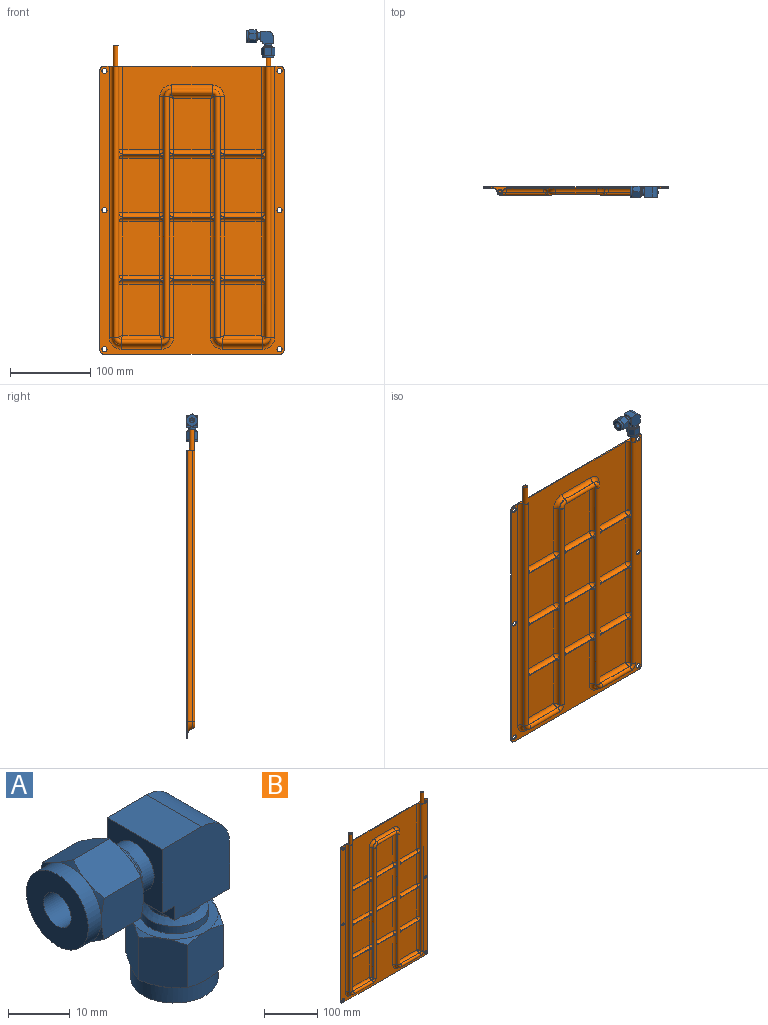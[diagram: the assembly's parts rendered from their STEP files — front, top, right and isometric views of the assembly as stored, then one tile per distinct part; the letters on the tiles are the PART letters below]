
ASSEMBLY  parts=2 mates=1
PART A: 64 faces, bbox 35.1x16.4x35.1 mm
  f0: cylinder r=3.17mm len=15.24mm, axis (1,0,0), area 304mm2, adj f1,f2
  f1: plane 6.35x6.35mm, normal (-1,0,0), area 13.4mm2, adj f0,f3
  f2: plane 14.22x14.22mm, normal (-1,0,0), area 127.2mm2, adj f0,f5
  f3: cylinder r=2.41mm len=11.68mm, axis (1,0,0), area 165.5mm2, adj f1,f4,f6
  f4: sphere r=2.41mm, area 18.3mm2, adj f3,f6
  f5: cylinder r=7.11mm len=14.22mm, axis (1,0,0), area 136.2mm2, adj f2,f7,f8,f9,f10,f11,f12
  f6: cylinder r=2.41mm len=11.68mm, axis (0,0,-1), area 165.5mm2, adj f3,f4,f13
  f7: cone r=7.66mm half-angle=60deg, axis (1,0,0), area 3.1mm2, adj f5,f14,f15
  f8: cone r=7.66mm half-angle=60deg, axis (1,0,0), area 3.1mm2, adj f5,f15,f16
  f9: cone r=7.66mm half-angle=60deg, axis (1,0,0), area 3.1mm2, adj f5,f16,f17
  f10: cone r=7.66mm half-angle=60deg, axis (1,0,0), area 3.1mm2, adj f5,f17,f18
  f11: cone r=7.66mm half-angle=60deg, axis (1,0,0), area 3.1mm2, adj f5,f18,f19
  f12: cone r=7.66mm half-angle=60deg, axis (1,0,0), area 3.1mm2, adj f5,f14,f19
  f13: plane 6.35x6.35mm, normal (0,0,-1), area 13.4mm2, adj f6,f20
  f14: plane 9.65x8.21mm, normal (0,1,0), area 75.7mm2, adj f7,f12,f15,f19,f21,f22
  f15: plane 9.65x7.11mm, normal (0,0.5,-0.87), area 75.7mm2, adj f7,f8,f14,f16,f22,f23
  f16: plane 9.65x7.11mm, normal (0,-0.5,-0.87), area 75.7mm2, adj f8,f9,f15,f17,f23,f24
  f17: plane 9.65x8.21mm, normal (0,-1,0), area 75.7mm2, adj f9,f10,f16,f18,f24,f25
  f18: plane 9.65x7.11mm, normal (0,-0.5,0.87), area 75.7mm2, adj f10,f11,f17,f19,f25,f26
  f19: plane 9.65x7.11mm, normal (0,0.5,0.87), area 75.7mm2, adj f11,f12,f14,f18,f21,f26
  f20: cylinder r=3.17mm len=15.24mm, axis (0,0,1), area 304mm2, adj f13,f27
  f21: cone r=7.66mm half-angle=60deg, axis (-1,0,0), area 3.1mm2, adj f14,f19,f28
  f22: cone r=7.66mm half-angle=60deg, axis (-1,0,0), area 3.1mm2, adj f14,f15,f28
  f23: cone r=7.66mm half-angle=60deg, axis (-1,0,0), area 3.1mm2, adj f15,f16,f28
  f24: cone r=7.66mm half-angle=60deg, axis (-1,0,0), area 3.1mm2, adj f16,f17,f28
  f25: cone r=7.66mm half-angle=60deg, axis (-1,0,0), area 3.1mm2, adj f17,f18,f28
  f26: cone r=7.66mm half-angle=60deg, axis (-1,0,0), area 3.1mm2, adj f18,f19,f28
  f27: plane 14.22x14.22mm, normal (0,0,-1), area 127.2mm2, adj f20,f29
  f28: plane 14.22x14.22mm, normal (1,0,0), area 61.9mm2, adj f21,f22,f23,f24,f25,f26,f30
  f29: cylinder r=7.11mm len=14.22mm, axis (0,0,1), area 136.2mm2, adj f27,f31,f32,f33,f34,f35,f36
  f30: cylinder r=5.56mm len=11.11mm, axis (1,0,0), area 51mm2, adj f28,f37
  f31: cone r=7.66mm half-angle=60deg, axis (0,0,1), area 3.1mm2, adj f29,f38,f39
  f32: cone r=7.66mm half-angle=60deg, axis (0,0,1), area 3.1mm2, adj f29,f39,f40
  f33: cone r=7.66mm half-angle=60deg, axis (0,0,1), area 3.1mm2, adj f29,f40,f41
  f34: cone r=7.66mm half-angle=60deg, axis (0,0,1), area 3.1mm2, adj f29,f41,f42
  f35: cone r=7.66mm half-angle=60deg, axis (0,0,1), area 3.1mm2, adj f29,f42,f43
  f36: cone r=7.66mm half-angle=60deg, axis (0,0,1), area 3.1mm2, adj f29,f38,f43
  f37: cone r=5.02mm half-angle=45deg, axis (-1,0,0), area 48.1mm2, adj f30,f44
  f38: plane 9.65x8.21mm, normal (0,1,0), area 75.7mm2, adj f31,f36,f39,f43,f45,f46
  f39: plane 9.65x7.11mm, normal (0.87,0.5,0), area 75.7mm2, adj f31,f32,f38,f40,f46,f47
  f40: plane 9.65x7.11mm, normal (0.87,-0.5,0), area 75.7mm2, adj f32,f33,f39,f41,f47,f48
  f41: plane 9.65x8.21mm, normal (0,-1,0), area 75.7mm2, adj f33,f34,f40,f42,f48,f49
  f42: plane 9.65x7.11mm, normal (-0.87,-0.5,0), area 75.7mm2, adj f34,f35,f41,f43,f49,f50
  f43: plane 9.65x7.11mm, normal (-0.87,0.5,0), area 75.7mm2, adj f35,f36,f38,f42,f45,f50
  f44: cylinder r=4.48mm len=8.95mm, axis (1,0,0), area 71.4mm2, adj f37,f52
  f45: cone r=7.66mm half-angle=60deg, axis (0,0,-1), area 3.1mm2, adj f38,f43,f55
  f46: cone r=7.66mm half-angle=60deg, axis (0,0,-1), area 3.1mm2, adj f38,f39,f55
  f47: cone r=7.66mm half-angle=60deg, axis (0,0,-1), area 3.1mm2, adj f39,f40,f55
  f48: cone r=7.66mm half-angle=60deg, axis (0,0,-1), area 3.1mm2, adj f40,f41,f55
  f49: cone r=7.66mm half-angle=60deg, axis (0,0,-1), area 3.1mm2, adj f41,f42,f55
  f50: cone r=7.66mm half-angle=60deg, axis (0,0,-1), area 3.1mm2, adj f42,f43,f55
  f51: plane 12.7x2.79mm, normal (0,0,-1), area 35.5mm2, adj f52,f57,f58,f59
  f52: plane 12.7x12.7mm, normal (-1,0,0), area 98.3mm2, adj f44,f51,f53,f57,f59
  f53: plane 12.7x9.14mm, normal (0,0,1), area 116.1mm2, adj f52,f54,f57,f59
  f54: cylinder r=6.35mm len=12.7mm, axis (0,-1,0), area 126.7mm2, adj f53,f57,f59,f60
  f55: plane 14.22x14.22mm, normal (0,0,1), area 61.9mm2, adj f45,f46,f47,f48,f49,f50,f56
  f56: cylinder r=5.56mm len=11.11mm, axis (0,0,1), area 51mm2, adj f55,f61
  f57: plane 15.49x15.49mm, normal (0,1,0), area 223.6mm2, adj f51,f52,f53,f54,f58,f60,f62
  f58: plane 12.7x2.79mm, normal (-1,0,0), area 35.5mm2, adj f51,f57,f59,f62
  f59: plane 15.49x15.49mm, normal (0,-1,0), area 223.6mm2, adj f51,f52,f53,f54,f58,f60,f62
  f60: plane 12.7x9.14mm, normal (1,0,0), area 116.1mm2, adj f54,f57,f59,f62
  f61: cone r=5.02mm half-angle=45deg, axis (0,0,-1), area 48.1mm2, adj f56,f63
  f62: plane 12.7x12.7mm, normal (0,0,-1), area 98.3mm2, adj f57,f58,f59,f60,f63
  f63: cylinder r=4.48mm len=8.95mm, axis (0,0,1), area 71.4mm2, adj f61,f62
PART B: 210 faces, bbox 230x9.8x385.4 mm
  f0: plane 67.51x46.06mm, normal (0,-1,0), area 3109.6mm2, adj f1,f2,f154,f157
  f1: cylinder r=5.21mm len=67.51mm, axis (0,0,-1), area 547mm2, adj f0,f88,f153,f158
  f2: cylinder r=5.21mm len=67.51mm, axis (0,0,1), area 547mm2, adj f0,f92,f155,f156
  f3: plane 66.49x46.06mm, normal (0,-1,0), area 3062.8mm2, adj f4,f5,f160,f163
  f4: cylinder r=5.21mm len=66.49mm, axis (0,0,-1), area 538.7mm2, adj f3,f88,f161,f164
  f5: cylinder r=5.21mm len=66.49mm, axis (0,0,1), area 538.7mm2, adj f3,f92,f159,f162
  f6: plane 360x230mm, normal (0,-1,0), area 13224.6mm2, adj f7,f8,f27,f31,f32,f33,f34,f35
  f7: cylinder r=5.21mm len=66.24mm, axis (0,0,-1), area 536.7mm2, adj f6,f88,f100,f167
  f8: cylinder r=5.21mm len=66.24mm, axis (0,0,1), area 536.7mm2, adj f6,f92,f106,f165
  f9: plane 67.51x46.06mm, normal (0,-1,0), area 3109.6mm2, adj f10,f11,f172,f181
  f10: cylinder r=5.21mm len=67.51mm, axis (0,0,1), area 547mm2, adj f9,f84,f173,f182
  f11: cylinder r=5.21mm len=67.51mm, axis (0,0,-1), area 547mm2, adj f9,f88,f171,f180
  f12: plane 67.51x46.06mm, normal (0,-1,0), area 3109.6mm2, adj f13,f14,f178,f187
  f13: cylinder r=5.21mm len=67.51mm, axis (0,0,1), area 547mm2, adj f12,f92,f177,f188
  f14: cylinder r=5.21mm len=67.51mm, axis (0,0,-1), area 547mm2, adj f12,f96,f179,f186
  f15: plane 66.49x46.06mm, normal (0,-1,0), area 3062.8mm2, adj f16,f17,f184,f193
  f16: cylinder r=5.21mm len=66.49mm, axis (0,0,1), area 538.7mm2, adj f15,f84,f185,f194
  f17: cylinder r=5.21mm len=66.49mm, axis (0,0,-1), area 538.7mm2, adj f15,f88,f183,f192
  f18: plane 66.49x46.06mm, normal (0,-1,0), area 3062.8mm2, adj f19,f20,f190,f199
  f19: cylinder r=5.21mm len=66.49mm, axis (0,0,1), area 538.7mm2, adj f18,f92,f189,f198
  f20: cylinder r=5.21mm len=66.49mm, axis (0,0,-1), area 538.7mm2, adj f18,f96,f191,f200
  f21: plane 63.95x46.06mm, normal (0,-1,0), area 2945.8mm2, adj f22,f23,f112,f196
  f22: cylinder r=5.21mm len=66.24mm, axis (0,0,1), area 527.4mm2, adj f21,f84,f111,f197
  f23: cylinder r=5.21mm len=66.24mm, axis (0,0,-1), area 527.4mm2, adj f21,f88,f113,f195
  f24: plane 63.95x46.06mm, normal (0,-1,0), area 2945.8mm2, adj f25,f26,f120,f202
  f25: cylinder r=5.21mm len=66.24mm, axis (0,0,1), area 527.4mm2, adj f24,f92,f119,f201
  f26: cylinder r=5.21mm len=66.24mm, axis (0,0,-1), area 527.4mm2, adj f24,f96,f122,f203
  f27: plane 220x9.78mm, normal (0,0,1), area 345.9mm2, adj f6,f33,f34,f38,f77,f80,f82,f84
  f28: plane 334.84x195.08mm, normal (0,-1,0), area 7435.3mm2, adj f29,f30,f40,f42,f43,f45,f46,f48
  f29: plane 325.95x3.81mm, normal (-1,0,0), area 1241.9mm2, adj f28,f39,f40,f78
  f30: plane 325.95x3.81mm, normal (1,0,0), area 1241.9mm2, adj f28,f39,f42,f78
  f31: plane 350x1.27mm, normal (-1,0,0), area 444.5mm2, adj f6,f34,f35,f38
  f32: cylinder r=5mm len=5mm, axis (0,1,0), area 10mm2, adj f6,f36,f37,f38
  f33: cylinder r=5mm len=5mm, axis (0,-1,0), area 10mm2, adj f6,f27,f37,f38
  f34: cylinder r=5mm len=5mm, axis (0,1,0), area 10mm2, adj f6,f27,f31,f38
  f35: cylinder r=5mm len=5mm, axis (0,-1,0), area 10mm2, adj f6,f31,f36,f38
  f36: plane 220x1.27mm, normal (0,0,-1), area 279.4mm2, adj f6,f32,f35,f38
  f37: plane 350x1.27mm, normal (1,0,0), area 444.5mm2, adj f6,f32,f33,f38
  f38: plane 360x230mm, normal (0,1,0), area 82588.5mm2, adj f27,f31,f32,f33,f34,f35,f36,f37
  f39: cylinder r=2.54mm len=364.05mm, axis (0,0,-1), area 3209mm2, adj f29,f30,f41,f78,f81
  f40: cylinder r=3.81mm len=3.81mm, axis (0,-1,0), area 22.8mm2, adj f28,f29,f41,f43
  f41: torus R=6.35mm, axis (0,-1,0), area 79.6mm2, adj f39,f40,f42,f44
  f42: cylinder r=8.89mm len=8.89mm, axis (0,-1,0), area 53.2mm2, adj f28,f30,f41,f45
  f43: plane 50.63x3.81mm, normal (0,0,-1), area 192.9mm2, adj f28,f40,f44,f46
  f44: cylinder r=2.54mm len=50.63mm, axis (1,0,0), area 404mm2, adj f41,f43,f45,f47
  f45: plane 50.63x3.81mm, normal (0,0,1), area 192.9mm2, adj f28,f42,f44,f48
  f46: cylinder r=3.81mm len=3.81mm, axis (0,-1,0), area 22.8mm2, adj f28,f43,f47,f49
  f47: torus R=6.35mm, axis (0,-1,0), area 79.6mm2, adj f44,f46,f48,f50
  f48: cylinder r=8.89mm len=8.89mm, axis (0,-1,0), area 53.2mm2, adj f28,f45,f47,f51
  f49: plane 300x3.81mm, normal (1,0,0), area 1143mm2, adj f28,f46,f50,f52
  f50: cylinder r=2.54mm len=300mm, axis (0,0,1), area 2393.9mm2, adj f47,f49,f51,f53
  f51: plane 300x3.81mm, normal (-1,0,0), area 1143mm2, adj f28,f48,f50,f54
  f52: cylinder r=8.89mm len=8.89mm, axis (0,1,0), area 53.2mm2, adj f28,f49,f53,f55
  f53: torus R=6.35mm, axis (0,1,0), area 79.6mm2, adj f50,f52,f54,f56
  f54: cylinder r=3.81mm len=3.81mm, axis (0,1,0), area 22.8mm2, adj f28,f51,f53,f57
  f55: plane 50.63x3.81mm, normal (0,0,-1), area 192.9mm2, adj f28,f52,f56,f58
  f56: cylinder r=2.54mm len=50.63mm, axis (1,0,0), area 404mm2, adj f53,f55,f57,f59
  f57: plane 50.63x3.81mm, normal (0,0,1), area 192.9mm2, adj f28,f54,f56,f60
  f58: cylinder r=8.89mm len=8.89mm, axis (0,1,0), area 53.2mm2, adj f28,f55,f59,f61
  f59: torus R=6.35mm, axis (0,1,0), area 79.6mm2, adj f56,f58,f60,f62
  f60: cylinder r=3.81mm len=3.81mm, axis (0,1,0), area 22.8mm2, adj f28,f57,f59,f63
  f61: plane 300x3.81mm, normal (-1,0,0), area 1143mm2, adj f28,f58,f62,f64
  f62: cylinder r=2.54mm len=300mm, axis (0,0,-1), area 2393.9mm2, adj f59,f61,f63,f65
  f63: plane 300x3.81mm, normal (1,0,0), area 1143mm2, adj f28,f60,f62,f66
  f64: cylinder r=3.81mm len=3.81mm, axis (0,-1,0), area 22.8mm2, adj f28,f61,f65,f67
  f65: torus R=6.35mm, axis (0,-1,0), area 79.6mm2, adj f62,f64,f66,f68
  f66: cylinder r=8.89mm len=8.89mm, axis (0,-1,0), area 53.2mm2, adj f28,f63,f65,f69
  f67: plane 50.63x3.81mm, normal (0,0,-1), area 192.9mm2, adj f28,f64,f68,f70
  f68: cylinder r=2.54mm len=50.63mm, axis (1,0,0), area 404mm2, adj f65,f67,f69,f71
  f69: plane 50.63x3.81mm, normal (0,0,1), area 192.9mm2, adj f28,f66,f68,f72
  f70: cylinder r=3.81mm len=3.81mm, axis (0,-1,0), area 22.8mm2, adj f28,f67,f71,f73
  f71: torus R=6.35mm, axis (0,-1,0), area 79.6mm2, adj f68,f70,f72,f74
  f72: cylinder r=8.89mm len=8.89mm, axis (0,-1,0), area 53.2mm2, adj f28,f69,f71,f75
  f73: plane 325.95x3.81mm, normal (1,0,0), area 1241.9mm2, adj f28,f70,f74,f79
  f74: cylinder r=2.54mm len=364.05mm, axis (0,0,1), area 3209mm2, adj f71,f73,f75,f79,f83
  f75: plane 325.95x3.81mm, normal (-1,0,0), area 1241.9mm2, adj f28,f72,f74,f79
  f76: plane 63.95x46.06mm, normal (0,-1,0), area 2945.8mm2, adj f101,f103,f105,f151
  f77: plane 172.73x104.89mm, normal (0,-1,0), area 11666.7mm2, adj f27,f110,f114,f115,f116,f117,f118,f121
  f78: plane 5.08x3.81mm, normal (0,0,-1), area 9.2mm2, adj f28,f29,f30,f39
  f79: plane 5.08x3.81mm, normal (0,0,-1), area 9.2mm2, adj f28,f73,f74,f75
  f80: cylinder r=3.17mm len=25.4mm, axis (0,0,-1), area 506.7mm2, adj f27,f81
  f81: plane 6.35x6.35mm, normal (0,0,1), area 11.4mm2, adj f39,f80
  f82: cylinder r=3.17mm len=25.4mm, axis (0,0,-1), area 506.7mm2, adj f27,f83
  f83: plane 6.35x6.35mm, normal (0,0,1), area 11.4mm2, adj f74,f82
  f84: cylinder r=3.43mm len=338.65mm, axis (0,0,1), area 3613.9mm2, adj f10,f16,f22,f27,f85,f97,f110,f128
  f85: torus R=6.35mm, axis (0,-1,0), area 106.4mm2, adj f84,f86,f98,f111
  f86: cylinder r=3.43mm len=50.63mm, axis (-1,0,0), area 540.3mm2, adj f85,f87,f99,f112
  f87: torus R=6.35mm, axis (0,-1,0), area 106.4mm2, adj f86,f88,f100,f113
  f88: cylinder r=3.43mm len=300mm, axis (0,0,-1), area 3201.5mm2, adj f1,f4,f7,f11,f17,f23,f87,f89
  f89: torus R=6.35mm, axis (0,-1,0), area 106.4mm2, adj f88,f90,f102,f115
  f90: cylinder r=3.43mm len=50.63mm, axis (-1,0,0), area 540.3mm2, adj f89,f91,f103,f116
  f91: torus R=6.35mm, axis (0,-1,0), area 106.4mm2, adj f90,f92,f104,f117
  f92: cylinder r=3.43mm len=300mm, axis (0,0,1), area 3201.5mm2, adj f2,f5,f8,f13,f19,f25,f91,f93
  f93: torus R=6.35mm, axis (0,-1,0), area 106.4mm2, adj f92,f94,f106,f119
  f94: cylinder r=3.43mm len=50.63mm, axis (-1,0,0), area 540.3mm2, adj f93,f95,f107,f120
  f95: torus R=6.35mm, axis (0,-1,0), area 106.4mm2, adj f94,f96,f108,f122
  f96: cylinder r=3.43mm len=338.65mm, axis (0,0,-1), area 3613.9mm2, adj f14,f20,f26,f27,f95,f109,f121,f125
  f97: cylinder r=5.21mm len=338.65mm, axis (0,0,1), area 2743.9mm2, adj f6,f27,f84,f98
  f98: torus R=14.99mm, axis (0,-1,0), area 148.8mm2, adj f6,f85,f97,f99
  f99: cylinder r=5.21mm len=50.63mm, axis (-1,0,0), area 410.3mm2, adj f6,f86,f98,f100
  f100: torus R=14.99mm, axis (0,-1,0), area 148.8mm2, adj f6,f7,f87,f99
  f101: cylinder r=5.21mm len=66.24mm, axis (0,0,-1), area 527.4mm2, adj f76,f88,f102,f152
  f102: bspline ~5.21x5.21mm, area 16.3mm2, adj f89,f101,f103
  f103: cylinder r=5.21mm len=50.63mm, axis (-1,0,0), area 391.7mm2, adj f76,f90,f102,f104
  f104: bspline ~5.21x5.21mm, area 16.3mm2, adj f91,f103,f105
  f105: cylinder r=5.21mm len=66.24mm, axis (0,0,1), area 527.4mm2, adj f76,f92,f104,f150
  f106: torus R=14.99mm, axis (0,-1,0), area 148.8mm2, adj f6,f8,f93,f107
  f107: cylinder r=5.21mm len=50.63mm, axis (-1,0,0), area 410.3mm2, adj f6,f94,f106,f108
  f108: torus R=14.99mm, axis (0,-1,0), area 148.8mm2, adj f6,f95,f107,f109
  f109: cylinder r=5.21mm len=338.65mm, axis (0,0,-1), area 2743.9mm2, adj f6,f27,f96,f108
  f110: cylinder r=5.21mm len=104.89mm, axis (0,0,1), area 849.9mm2, adj f27,f77,f84,f170
  f111: bspline ~5.21x5.21mm, area 16.3mm2, adj f22,f85,f112
  f112: cylinder r=5.21mm len=50.63mm, axis (-1,0,0), area 391.7mm2, adj f21,f86,f111,f113
  f113: bspline ~5.21x5.21mm, area 16.3mm2, adj f23,f87,f112
  f114: cylinder r=5.21mm len=66.24mm, axis (0,0,-1), area 536.7mm2, adj f77,f88,f115,f168
  f115: torus R=14.99mm, axis (0,-1,0), area 148.8mm2, adj f77,f89,f114,f116
  f116: cylinder r=5.21mm len=50.63mm, axis (-1,0,0), area 410.3mm2, adj f77,f90,f115,f117
  f117: torus R=14.99mm, axis (0,-1,0), area 148.8mm2, adj f77,f91,f116,f118
  f118: cylinder r=5.21mm len=66.24mm, axis (0,0,1), area 536.7mm2, adj f77,f92,f117,f176
  f119: bspline ~5.21x5.21mm, area 16.3mm2, adj f25,f93,f120
  f120: cylinder r=5.21mm len=50.63mm, axis (-1,0,0), area 391.7mm2, adj f24,f94,f119,f122
  f121: cylinder r=5.21mm len=104.89mm, axis (0,0,-1), area 849.9mm2, adj f27,f77,f96,f174
  f122: bspline ~5.21x5.21mm, area 16.3mm2, adj f26,f95,f120
  f123: plane 46.27x0.05mm, normal (0,0,-1), area 2.3mm2, adj f125,f201,f202,f203
  f124: plane 46.27x0.05mm, normal (0,0,1), area 2.3mm2, adj f125,f198,f199,f200
  f125: plane 56.48x11.18mm, normal (0,-1,0), area 79.5mm2, adj f92,f96,f123,f124,f198,f200,f201,f203
  f126: plane 46.27x0.05mm, normal (0,0,1), area 2.3mm2, adj f128,f192,f193,f194
  f127: plane 46.27x0.05mm, normal (0,0,-1), area 2.3mm2, adj f128,f195,f196,f197
  f128: plane 56.48x11.18mm, normal (0,-1,0), area 79.5mm2, adj f84,f88,f126,f127,f192,f194,f195,f197
  f129: plane 46.27x0.05mm, normal (0,0,-1), area 2.3mm2, adj f131,f189,f190,f191
  f130: plane 46.27x0.05mm, normal (0,0,1), area 2.3mm2, adj f131,f186,f187,f188
  f131: plane 56.48x11.18mm, normal (0,-1,0), area 79.5mm2, adj f92,f96,f129,f130,f186,f188,f189,f191
  f132: plane 46.27x0.05mm, normal (0,0,1), area 2.3mm2, adj f134,f180,f181,f182
  f133: plane 46.27x0.05mm, normal (0,0,-1), area 2.3mm2, adj f134,f183,f184,f185
  f134: plane 56.48x11.18mm, normal (0,-1,0), area 79.5mm2, adj f84,f88,f132,f133,f180,f182,f183,f185
  f135: plane 46.27x0.05mm, normal (0,0,-1), area 2.3mm2, adj f137,f177,f178,f179
  f136: plane 46.27x0.05mm, normal (0,0,1), area 2.3mm2, adj f137,f174,f175,f176
  f137: plane 56.48x11.18mm, normal (0,-1,0), area 79.5mm2, adj f92,f96,f135,f136,f174,f176,f177,f179
  f138: plane 46.27x0.05mm, normal (0,0,1), area 2.3mm2, adj f140,f168,f169,f170
  f139: plane 46.27x0.05mm, normal (0,0,-1), area 2.3mm2, adj f140,f171,f172,f173
  f140: plane 56.48x11.18mm, normal (0,-1,0), area 79.5mm2, adj f84,f88,f138,f139,f168,f170,f171,f173
  f141: plane 46.27x0.05mm, normal (0,0,-1), area 2.3mm2, adj f143,f165,f166,f167
  f142: plane 46.27x0.05mm, normal (0,0,1), area 2.3mm2, adj f143,f162,f163,f164
  f143: plane 56.48x11.18mm, normal (0,-1,0), area 79.5mm2, adj f88,f92,f141,f142,f162,f164,f165,f167
  f144: plane 46.27x0.05mm, normal (0,0,-1), area 2.3mm2, adj f146,f159,f160,f161
  f145: plane 46.27x0.05mm, normal (0,0,1), area 2.3mm2, adj f146,f156,f157,f158
  f146: plane 56.48x11.18mm, normal (0,-1,0), area 79.5mm2, adj f88,f92,f144,f145,f156,f158,f159,f161
  f147: plane 46.27x0.05mm, normal (0,0,-1), area 2.3mm2, adj f149,f153,f154,f155
  f148: plane 46.27x0.05mm, normal (0,0,1), area 2.3mm2, adj f149,f150,f151,f152
  f149: plane 56.48x11.18mm, normal (0,-1,0), area 79.5mm2, adj f88,f92,f147,f148,f150,f152,f153,f155
  f150: torus R=0.13mm, axis (0,0,-1), area 41.5mm2, adj f105,f148,f149,f151
  f151: cylinder r=5.08mm len=46.06mm, axis (-1,0,0), area 367.6mm2, adj f76,f148,f150,f152
  f152: torus R=0.13mm, axis (0,0,-1), area 41.5mm2, adj f101,f148,f149,f151
  f153: torus R=0.13mm, axis (0,0,-1), area 41.5mm2, adj f1,f147,f149,f154
  f154: cylinder r=5.08mm len=46.06mm, axis (1,0,0), area 367.6mm2, adj f0,f147,f153,f155
  f155: torus R=0.13mm, axis (0,0,-1), area 41.5mm2, adj f2,f147,f149,f154
  f156: torus R=0.13mm, axis (0,0,-1), area 41.5mm2, adj f2,f145,f146,f157
  f157: cylinder r=5.08mm len=46.06mm, axis (-1,0,0), area 367.6mm2, adj f0,f145,f156,f158
  f158: torus R=0.13mm, axis (0,0,-1), area 41.5mm2, adj f1,f145,f146,f157
  f159: torus R=0.13mm, axis (0,0,-1), area 41.5mm2, adj f5,f144,f146,f160
  f160: cylinder r=5.08mm len=46.06mm, axis (1,0,0), area 367.6mm2, adj f3,f144,f159,f161
  f161: torus R=0.13mm, axis (0,0,-1), area 41.5mm2, adj f4,f144,f146,f160
  f162: torus R=0.13mm, axis (0,0,-1), area 41.5mm2, adj f5,f142,f143,f163
  f163: cylinder r=5.08mm len=46.06mm, axis (-1,0,0), area 367.6mm2, adj f3,f142,f162,f164
  f164: torus R=0.13mm, axis (0,0,-1), area 41.5mm2, adj f4,f142,f143,f163
  f165: torus R=0.13mm, axis (0,0,-1), area 41.5mm2, adj f8,f141,f143,f166
  f166: cylinder r=5.08mm len=46.06mm, axis (1,0,0), area 367.6mm2, adj f6,f141,f165,f167
  f167: torus R=0.13mm, axis (0,0,-1), area 41.5mm2, adj f7,f141,f143,f166
  f168: torus R=0.13mm, axis (0,0,-1), area 41.5mm2, adj f114,f138,f140,f169
  f169: cylinder r=5.08mm len=46.06mm, axis (-1,0,0), area 367.6mm2, adj f77,f138,f168,f170
  f170: torus R=0.13mm, axis (0,0,-1), area 41.5mm2, adj f110,f138,f140,f169
  f171: torus R=0.13mm, axis (0,0,-1), area 41.5mm2, adj f11,f139,f140,f172
  f172: cylinder r=5.08mm len=46.06mm, axis (1,0,0), area 367.6mm2, adj f9,f139,f171,f173
  f173: torus R=0.13mm, axis (0,0,-1), area 41.5mm2, adj f10,f139,f140,f172
  f174: torus R=0.13mm, axis (0,0,-1), area 41.5mm2, adj f121,f136,f137,f175
  f175: cylinder r=5.08mm len=46.06mm, axis (-1,0,0), area 367.6mm2, adj f77,f136,f174,f176
  f176: torus R=0.13mm, axis (0,0,-1), area 41.5mm2, adj f118,f136,f137,f175
  f177: torus R=0.13mm, axis (0,0,-1), area 41.5mm2, adj f13,f135,f137,f178
  f178: cylinder r=5.08mm len=46.06mm, axis (1,0,0), area 367.6mm2, adj f12,f135,f177,f179
  f179: torus R=0.13mm, axis (0,0,-1), area 41.5mm2, adj f14,f135,f137,f178
  f180: torus R=0.13mm, axis (0,0,-1), area 41.5mm2, adj f11,f132,f134,f181
  f181: cylinder r=5.08mm len=46.06mm, axis (-1,0,0), area 367.6mm2, adj f9,f132,f180,f182
  f182: torus R=0.13mm, axis (0,0,-1), area 41.5mm2, adj f10,f132,f134,f181
  f183: torus R=0.13mm, axis (0,0,-1), area 41.5mm2, adj f17,f133,f134,f184
  f184: cylinder r=5.08mm len=46.06mm, axis (1,0,0), area 367.6mm2, adj f15,f133,f183,f185
  f185: torus R=0.13mm, axis (0,0,-1), area 41.5mm2, adj f16,f133,f134,f184
  f186: torus R=0.13mm, axis (0,0,-1), area 41.5mm2, adj f14,f130,f131,f187
  f187: cylinder r=5.08mm len=46.06mm, axis (-1,0,0), area 367.6mm2, adj f12,f130,f186,f188
  f188: torus R=0.13mm, axis (0,0,-1), area 41.5mm2, adj f13,f130,f131,f187
  f189: torus R=0.13mm, axis (0,0,-1), area 41.5mm2, adj f19,f129,f131,f190
  f190: cylinder r=5.08mm len=46.06mm, axis (1,0,0), area 367.6mm2, adj f18,f129,f189,f191
  f191: torus R=0.13mm, axis (0,0,-1), area 41.5mm2, adj f20,f129,f131,f190
  f192: torus R=0.13mm, axis (0,0,-1), area 41.5mm2, adj f17,f126,f128,f193
  f193: cylinder r=5.08mm len=46.06mm, axis (-1,0,0), area 367.6mm2, adj f15,f126,f192,f194
  f194: torus R=0.13mm, axis (0,0,-1), area 41.5mm2, adj f16,f126,f128,f193
  f195: torus R=0.13mm, axis (0,0,-1), area 41.5mm2, adj f23,f127,f128,f196
  f196: cylinder r=5.08mm len=46.06mm, axis (1,0,0), area 367.6mm2, adj f21,f127,f195,f197
  f197: torus R=0.13mm, axis (0,0,-1), area 41.5mm2, adj f22,f127,f128,f196
  f198: torus R=0.13mm, axis (0,0,-1), area 41.5mm2, adj f19,f124,f125,f199
  f199: cylinder r=5.08mm len=46.06mm, axis (-1,0,0), area 367.6mm2, adj f18,f124,f198,f200
  f200: torus R=0.13mm, axis (0,0,-1), area 41.5mm2, adj f20,f124,f125,f199
  f201: torus R=0.13mm, axis (0,0,-1), area 41.5mm2, adj f25,f123,f125,f202
  f202: cylinder r=5.08mm len=46.06mm, axis (1,0,0), area 367.6mm2, adj f24,f123,f201,f203
  f203: torus R=0.13mm, axis (0,0,-1), area 41.5mm2, adj f26,f123,f125,f202
  f204: cylinder r=3.17mm len=6.35mm, axis (0,-1,0), area 25.3mm2, adj f6,f38
  f205: cylinder r=3.17mm len=6.35mm, axis (0,-1,0), area 25.3mm2, adj f6,f38
  f206: cylinder r=3.17mm len=6.35mm, axis (0,-1,0), area 25.3mm2, adj f6,f38
  f207: cylinder r=3.17mm len=6.35mm, axis (0,-1,0), area 25.3mm2, adj f6,f38
  f208: cylinder r=3.17mm len=6.35mm, axis (0,-1,0), area 25.3mm2, adj f6,f38
  f209: cylinder r=3.17mm len=6.35mm, axis (0,-1,0), area 25.3mm2, adj f6,f38
PLACE A t=(11.68,-14.32,233.93)mm
PLACE B t=(-56.4,-12.86,16.85)mm
MATE fastened A.f63 <-> B.f82  axis (0,0,-1) through (38.6,-14.32,222.25)mm
